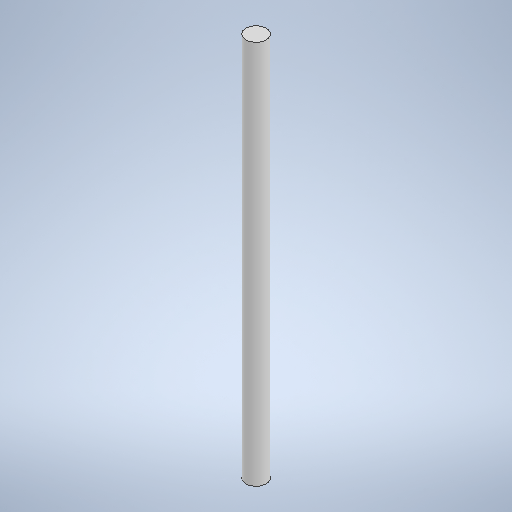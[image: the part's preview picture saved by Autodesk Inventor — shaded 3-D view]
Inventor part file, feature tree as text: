
AUTODESK INVENTOR PART (.ipt)
format: ipt  version: 2025.2 (Build 292293000, 293)  size: 248,832 bytes
history: native  units: in
note: dims shown in document units (in); Inventor stores cm internally (conversion verified against a paired STEP export)
features: extrude x1, sketch x1
ambient origin geometry x8: Origin, YZ Plane, XZ Plane, XY Plane, X Axis, Y Axis, Z Axis, Center Point
bodies: Body1 (feature_tree)
feature tree (2):
  extrude  "Extrusion2"  Depth=1.4094in TaperAngle=0.0deg
  sketch  "Sketch2"  dims[d3=0.0748in d4=1.4094in d5=0.0in]
